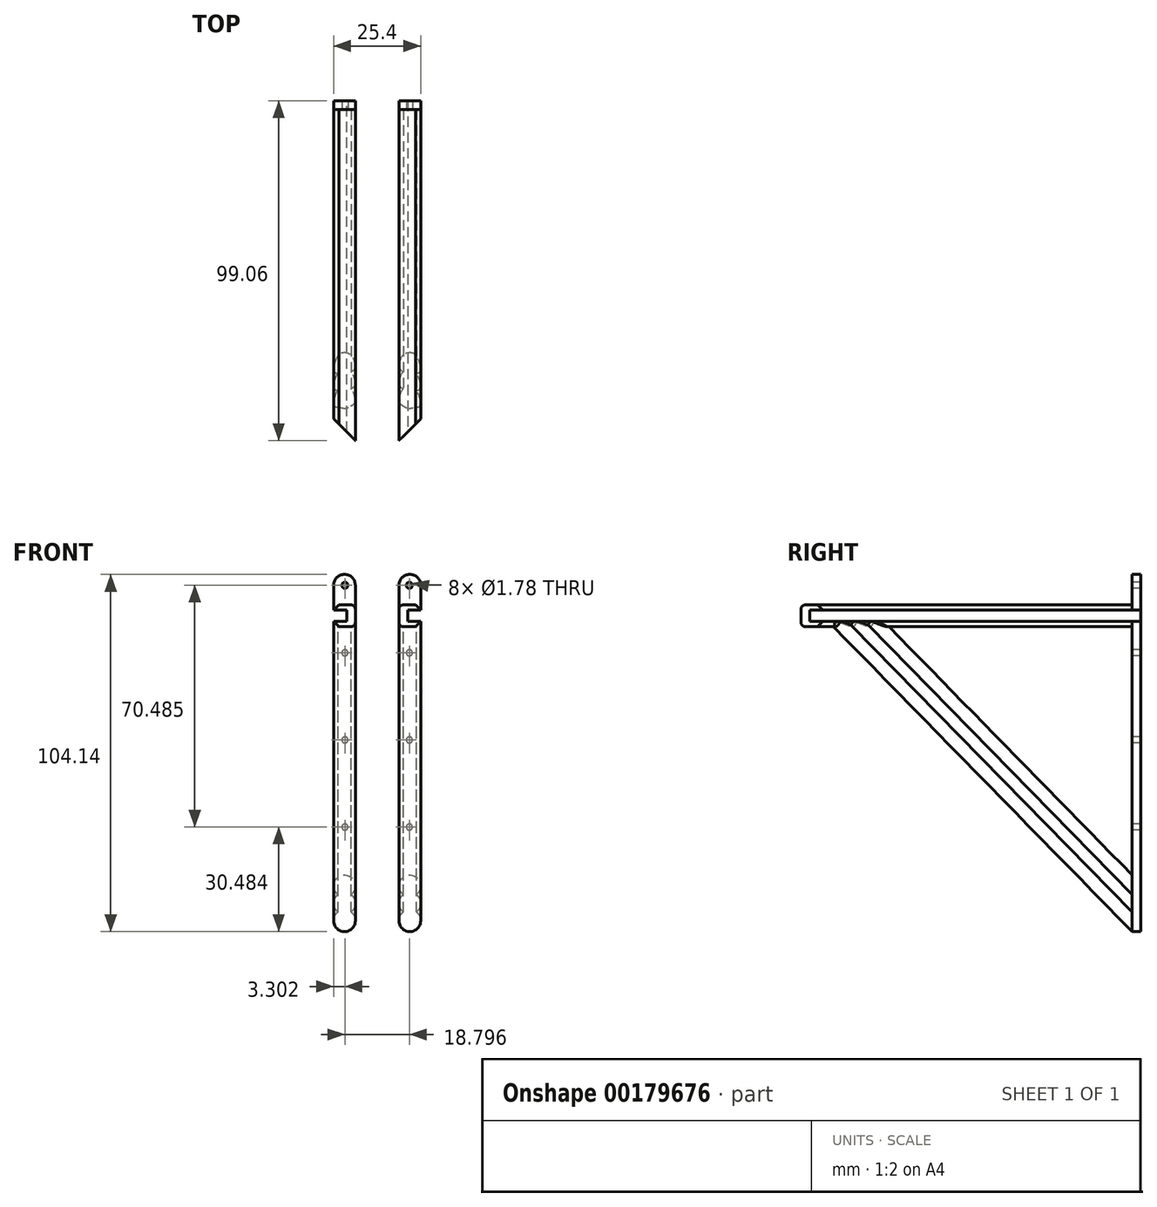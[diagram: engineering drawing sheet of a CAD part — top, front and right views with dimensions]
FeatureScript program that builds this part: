
annotation { "Feature Type Name" : "Feature", "Feature Type Description" : "" }
export const myFeature = defineFeature(function(context is Context, id is Id, definition is map)
    precondition{}
    {
        {
            var Q0;
            Q0=qCreatedBy(makeId("Right.planeOp"),FACE);
            var sketch = newSketch(context, id + "F0", { "sketchPlane" : qUnion([Q0])});
            skLineSegment(sketch, "E0.bottom", {"start": v(-5.81, 6.3) * mm, "end": v(90.7, 6.3) * mm});
            skLineSegment(sketch, "E0.top", {"start": v(-5.81, -0.06) * mm, "end": v(90.7, -0.06) * mm});
            skLineSegment(sketch, "E0.left", {"start": v(-5.81, 6.3) * mm, "end": v(-5.81, -0.06) * mm});
            skLineSegment(sketch, "E0.right", {"start": v(90.7, 6.3) * mm, "end": v(90.7, -0.06) * mm});
            skSolve(sketch);
        }
        {
            var Q0;
            Q0 = qSketchRegion(id + "F0", true);
            extrude(context, id + "F1", {"entities" : qUnion([Q0]), "depth" : 2.54 * mm});
        }
        {
            var Q0;
            Q0=makeQuery(id+"F1.opExtrude","CAP_FACE",FACE,{"disambiguationData":[OSD([sQuery(id+"F0.wireOp",EDGE,"E0.bottom"),sQuery(id+"F0.wireOp",EDGE,"E0.top"),sQuery(id+"F0.wireOp",EDGE,"E0.left"),sQuery(id+"F0.wireOp",EDGE,"E0.right")])],"isStart":false});
            var sketch = newSketch(context, id + "F2", { "sketchPlane" : qUnion([Q0])});
            skLineSegment(sketch, "E1.bottom", {"start": v(-5.81, 6.3) * mm, "end": v(90.7, 6.3) * mm});
            skLineSegment(sketch, "E1.top", {"start": v(-5.81, 4.77) * mm, "end": v(90.7, 4.77) * mm});
            skLineSegment(sketch, "E1.left", {"start": v(-5.81, 6.3) * mm, "end": v(-5.81, 4.77) * mm});
            skLineSegment(sketch, "E1.right", {"start": v(90.7, 6.3) * mm, "end": v(90.7, 4.77) * mm});
            skLineSegment(sketch, "E2.bottom", {"start": v(90.7, -0.06) * mm, "end": v(-5.81, -0.06) * mm});
            skLineSegment(sketch, "E2.top", {"start": v(90.7, 1.52) * mm, "end": v(-5.81, 1.52) * mm});
            skLineSegment(sketch, "E2.left", {"start": v(90.7, -0.06) * mm, "end": v(90.7, 1.52) * mm});
            skLineSegment(sketch, "E2.right", {"start": v(-5.81, -0.06) * mm, "end": v(-5.81, 1.52) * mm});
            skSolve(sketch);
        }
        {
            var Q0;
            Q0 = qSketchRegion(id + "F2", true);
            extrude(context, id + "F3", {"entities" : qUnion([Q0]), "operationType" : NewBodyOperationType.ADD, "depth" : 3.8 * mm});
        }
        {
            var Q0;
            Q0=makeQuery(id+"F3.boolean.opBoolean","MERGE",FACE,{"derivedFrom":[makeQuery(id+"F1.opExtrude","SWEPT_FACE",FACE,{"disambiguationData":[OSD([sQuery(id+"F0.wireOp",EDGE,"E0.bottom")])]}),makeQuery(id+"F3.opExtrude","SWEPT_FACE",FACE,{"disambiguationData":[OSD([sQuery(id+"F2.wireOp",EDGE,"E1.bottom")])]})]});
            var sketch = newSketch(context, id + "F4", { "sketchPlane" : qUnion([Q0])});
            skLineSegment(sketch, "E3", {"start": v(0, -5.81) * mm, "end": v(12.7, -5.81) * mm});
            skLineSegment(sketch, "E4", {"start": v(12.7, -5.81) * mm, "end": v(12.7, 6.89) * mm});
            skLineSegment(sketch, "E5", {"start": v(12.7, 6.89) * mm, "end": v(0, -5.81) * mm});
            skSolve(sketch);
        }
        {
            var Q0;
            Q0 = qSketchRegion(id + "F4", true);
            extrude(context, id + "F5", {"entities" : qUnion([Q0]), "operationType" : NewBodyOperationType.REMOVE, "endBound" : BoundingType.THROUGH_ALL, "oppositeDirection" : true, "depth" : 25.4 * mm});
        }
        {
            var Q0;
            Q0=makeQuery(id+"F3.opExtrude","CAP_EDGE",EDGE,{"disambiguationData":[OSD([sQuery(id+"F2.wireOp",EDGE,"E1.bottom")])],"isStart":false});
            var Q1;
            Q1=makeQuery(id+"F3.opExtrude","CAP_EDGE",EDGE,{"disambiguationData":[OSD([sQuery(id+"F2.wireOp",EDGE,"E2.bottom")])],"isStart":false});
            chamfer(context, id + "F6", {"entities" : qUnion([Q0, Q1]), "width" : 1.52 * mm});
        }
        {
            var Q0;
            Q0=makeQuery(id+"F1.opExtrude","CAP_EDGE",EDGE,{"disambiguationData":[OSD([sQuery(id+"F0.wireOp",EDGE,"E0.bottom")])],"isStart":true});
            var Q1;
            Q1=makeQuery(id+"F1.opExtrude","CAP_EDGE",EDGE,{"disambiguationData":[OSD([sQuery(id+"F0.wireOp",EDGE,"E0.top")])],"isStart":true});
            fillet(context, id + "F7", {"entities" : qUnion([Q0, Q1]), "radius" : 1.27 * mm, "tangentPropagation" : true, "allowEdgeOverflow" : false});
        }
        {
            var Q0;
            Q0=makeQuery(id+"F3.boolean.opBoolean","MERGE",FACE,{"derivedFrom":[makeQuery(id+"F1.opExtrude","SWEPT_FACE",FACE,{"disambiguationData":[OSD([sQuery(id+"F0.wireOp",EDGE,"E0.right")])]}),makeQuery(id+"F3.opExtrude","SWEPT_FACE",FACE,{"disambiguationData":[OSD([sQuery(id+"F2.wireOp",EDGE,"E1.right")])]}),makeQuery(id+"F3.opExtrude","SWEPT_FACE",FACE,{"disambiguationData":[OSD([sQuery(id+"F2.wireOp",EDGE,"E2.left")])]})]});
            var sketch = newSketch(context, id + "F8", { "sketchPlane" : qUnion([Q0])});
            skLineSegment(sketch, "E6.bottom", {"start": v(0, 15.18) * mm, "end": v(-6.35, 15.18) * mm});
            skLineSegment(sketch, "E6.top", {"start": v(0, -88.96) * mm, "end": v(-6.35, -88.96) * mm});
            skLineSegment(sketch, "E6.left", {"start": v(0, 15.18) * mm, "end": v(0, -88.96) * mm});
            skLineSegment(sketch, "E6.right", {"start": v(-6.35, 15.18) * mm, "end": v(-6.35, -88.96) * mm});
            skSolve(sketch);
        }
        {
            var Q0;
            {var subQ6=sQuery(id+"F8.wireOp",EDGE,"E6.top");Q0=makeQuery(id+"F8.imprint","IMPRINT",FACE,{"disambiguationData":[TD([[makeQuery(id+"F8.imprint","IMPRINT",EDGE,{"derivedFrom":subQ6}),-1.0]])]});}
            var Q1;
            {var subQ6=sQuery(id+"F8.wireOp",EDGE,"E6.bottom");Q1=makeQuery(id+"F8.imprint","IMPRINT",FACE,{"disambiguationData":[TD([[makeQuery(id+"F8.imprint","IMPRINT",EDGE,{"derivedFrom":subQ6}),1.0]])]});}
            var Q2;
            {var subQ2=sQuery(id+"F0.wireOp",EDGE,"E0.right");Q2=makeQuery(id+"F8.imprint","IMPRINT",FACE,{"disambiguationData":[TD([[makeQuery(id+"F8.imprint","IMPRINT",EDGE,{"derivedFrom":makeQuery(id+"F1.opExtrude","CAP_EDGE",EDGE,{"disambiguationData":[OSD([subQ2])],"isStart":false})}),1.0]])]});}
            extrude(context, id + "F9", {"entities" : qUnion([Q0, Q1, Q2]), "operationType" : NewBodyOperationType.ADD, "depth" : 2.54 * mm});
        }
        {
            var Q0;
            {var subQ1=sQuery(id+"F0.wireOp",EDGE,"E0.top");var subQ2=sQuery(id+"F2.wireOp",EDGE,"E2.left");var subQ3=sQuery(id+"F2.wireOp",EDGE,"E2.top");var subQ4=sQuery(id+"F0.wireOp",EDGE,"E0.right");var subQ5=sQuery(id+"F8.wireOp",EDGE,"E6.top");var subQ6=sQuery(id+"F8.wireOp",EDGE,"E6.left");var subQ7=sQuery(id+"F8.wireOp",EDGE,"E6.right");var subQ8=sQuery(id+"F2.wireOp",EDGE,"E1.right");Q0=makeQuery(id+"F9.boolean.opBoolean","SPLIT",FACE,{"disambiguationData":[TD([makeQuery(id+"F1.opExtrude","SWEPT_FACE",FACE,{"disambiguationData":[OSD([subQ1])]})])],"derivedFrom":makeQuery(id+"F9.opExtrude","CAP_FACE",FACE,{"disambiguationData":[OSD([subQ4,sQuery(id+"F2.wireOp",EDGE,"E1.top"),subQ8,subQ3,subQ2,sQuery(id+"F8.wireOp",EDGE,"E6.bottom"),subQ5,subQ6,subQ7])],"isStart":true})});}
            var sketch = newSketch(context, id + "F10", { "sketchPlane" : qUnion([Q0])});
            skArc(sketch, "E7", {"start": v(1.27, -83.24) * mm, "mid": v(3.17, -88.96) * mm, "end": v(5.08, -83.24) * mm});
            skPoint(sketch, "E7.centerSnap0", {"position": v(3.18, -88.96) * mm});
            skArc(sketch, "E8", {"start": v(5.08, -83.24) * mm, "mid": v(6.35, -80.7) * mm, "end": v(5.08, -78.16) * mm});
            skArc(sketch, "E9", {"start": v(5.08, -78.16) * mm, "mid": v(3.17, -72.45) * mm, "end": v(1.27, -78.16) * mm});
            skPoint(sketch, "E9.centerSnap0", {"position": v(3.17, -77.53) * mm});
            skArc(sketch, "E10.trimOffspring", {"start": v(1.27, -78.16) * mm, "mid": v(0, -80.7) * mm, "end": v(1.27, -83.24) * mm});
            skSolve(sketch);
        }
        {
            var Q0;
            {var subQ0=sQuery(id+"F8.wireOp",EDGE,"E6.right");var subQ1=sQuery(id+"F2.wireOp",EDGE,"E2.left");var subQ2=sQuery(id+"F2.wireOp",EDGE,"E2.top");var subQ3=sQuery(id+"F0.wireOp",EDGE,"E0.right");var subQ4=sQuery(id+"F2.wireOp",EDGE,"E2.bottom");Q0=makeQuery(id+"F9.boolean.opBoolean","MERGE",FACE,{"derivedFrom":[makeQuery(id+"F3.opExtrude","CAP_FACE",FACE,{"disambiguationData":[OSD([subQ4,subQ2,subQ1,sQuery(id+"F2.wireOp",EDGE,"E2.right")])],"isStart":false}),makeQuery(id+"F9.opExtrude","SWEPT_FACE",FACE,{"disambiguationData":[OSD([subQ0]),TDD([makeQuery(id+"F8.imprint","IMPRINT",EDGE,{"disambiguationData":[TD([[makeQuery(id+"F8.imprint","INTERSECT",VERTEX,{"derivedFrom":[sQuery(id+"F8.wireOp",EDGE,"E6.top"),subQ0]}),1.0]])],"derivedFrom":subQ0}),makeQuery(id+"F8.imprint","IMPRINT",EDGE,{"disambiguationData":[TD([[makeQuery(id+"F8.imprint","INTERSECT",VERTEX,{"derivedFrom":[makeQuery(id+"F3.opExtrude","SWEPT_EDGE",EDGE,{"disambiguationData":[OSD([subQ3,subQ2,subQ1])]}),subQ0]}),-1.0]])],"derivedFrom":subQ0})])]})]});}
            var Q1;
            Q1=makeQuery(id+"F9.boolean.opBoolean","MERGE",FACE,{"derivedFrom":[makeQuery(id+"F1.opExtrude","CAP_FACE",FACE,{"disambiguationData":[OSD([sQuery(id+"F0.wireOp",EDGE,"E0.bottom"),sQuery(id+"F0.wireOp",EDGE,"E0.top"),sQuery(id+"F0.wireOp",EDGE,"E0.left"),sQuery(id+"F0.wireOp",EDGE,"E0.right")])],"isStart":true}),makeQuery(id+"F9.opExtrude","SWEPT_FACE",FACE,{"disambiguationData":[OSD([sQuery(id+"F8.wireOp",EDGE,"E6.left")])]})]});
            cPlane(context, id + "F11", {"entities" : qUnion([Q0, Q1]), "cplaneType" : CPlaneType.MID_PLANE, "offset" : 25.4 * mm, "width" : 152.4 * mm, "height" : 152.4 * mm});
        }
        {
            var Q0;
            Q0=qCreatedBy(id+"F11.planeOp",FACE);
            var sketch = newSketch(context, id + "F12", { "sketchPlane" : qUnion([Q0])});
            skLineSegment(sketch, "E11", {"start": v(90.7, -88.96) * mm, "end": v(3.58, 0) * mm});
            skSolve(sketch);
        }
        {
            var Q0;
            {var subQ1=sQuery(id+"F10.wireOp",EDGE,"E7");var subQ9=sQuery(id+"F8.wireOp",EDGE,"E6.top");var subQ12=makeQuery(id+"F10.imprint","INTERSECT",VERTEX,{"derivedFrom":[makeQuery(id+"F9.opExtrude","CAP_EDGE",EDGE,{"disambiguationData":[OSD([subQ9])],"isStart":true}),subQ1]});Q0=makeQuery(id+"F10.imprint","IMPRINT",FACE,{"disambiguationData":[TD([[makeQuery(id+"F10.imprint","IMPRINT",EDGE,{"disambiguationData":[TD([[subQ12,-1.0]])],"derivedFrom":subQ1}),1.0]])]});}
            var Q1;
            Q1=sQuery(id+"F12.wireOp",EDGE,"E11");
            sweep(context, id + "F13", {"operationType" : NewBodyOperationType.ADD, "profiles" : qUnion([Q0]), "path" : qUnion([Q1])});
        }
        {
            var Q0;
            {var subQ0=sQuery(id+"F2.wireOp",EDGE,"E1.top");var subQ3=sQuery(id+"F10.wireOp",EDGE,"E7");Q0=makeQuery(id+"F13.boolean.opBoolean","SPLIT",FACE,{"disambiguationData":[TD([makeQuery(id+"F3.opExtrude","SWEPT_FACE",FACE,{"disambiguationData":[OSD([subQ0])]})])],"derivedFrom":makeQuery(id+"F13.opSweep","CAP_FACE",FACE,{"disambiguationData":[OSD([subQ3,sQuery(id+"F10.wireOp",EDGE,"E8"),sQuery(id+"F12.wireOp",VERTEX,"E11.end")])],"isStart":false})});}
            var sketch = newSketch(context, id + "F14", { "sketchPlane" : qUnion([Q0])});
            skLineSegment(sketch, "E12", {"start": v(6.35, 4.77) * mm, "end": v(2.54, 4.77) * mm});
            skLineSegment(sketch, "E13", {"start": v(2.54, 4.77) * mm, "end": v(2.54, 1.52) * mm});
            skLineSegment(sketch, "E14", {"start": v(2.54, 1.52) * mm, "end": v(6.35, 1.52) * mm});
            skLineSegment(sketch, "E15", {"start": v(6.35, 1.52) * mm, "end": v(8.34, 2.97) * mm});
            skLineSegment(sketch, "E16", {"start": v(8.34, 2.97) * mm, "end": v(6.35, 4.77) * mm});
            skLineSegment(sketch, "E17", {"start": v(6.35, 4.77) * mm, "end": v(4.83, 6.3) * mm});
            skLineSegment(sketch, "E18", {"start": v(4.83, 6.3) * mm, "end": v(1.27, 6.3) * mm});
            skArc(sketch, "E19", {"start": v(1.27, 6.3) * mm, "mid": v(0.37, 5.92) * mm, "end": v(0, 5.02) * mm});
            skLineSegment(sketch, "E20", {"start": v(0, 5.02) * mm, "end": v(0, 17.72) * mm});
            skLineSegment(sketch, "E21", {"start": v(0, 17.72) * mm, "end": v(9.04, 18.27) * mm});
            skLineSegment(sketch, "E22", {"start": v(9.04, 18.27) * mm, "end": v(6.35, 4.77) * mm});
            skSolve(sketch);
        }
        {
            var Q0;
            Q0 = qSketchRegion(id + "F14", true);
            extrude(context, id + "F15", {"entities" : qUnion([Q0]), "operationType" : NewBodyOperationType.REMOVE, "oppositeDirection" : true, "depth" : 25.4 * mm});
        }
        {
            var Q0;
            {var subQ0=sQuery(id+"F2.wireOp",EDGE,"E2.bottom");var subQ1=makeQuery(id+"F3.opExtrude","SWEPT_FACE",FACE,{"disambiguationData":[OSD([subQ0])]});var subQ2=sQuery(id+"F8.wireOp",EDGE,"E6.right");var subQ3=sQuery(id+"F8.wireOp",EDGE,"E6.left");var subQ4=sQuery(id+"F8.wireOp",EDGE,"E6.top");var subQ5=sQuery(id+"F2.wireOp",EDGE,"E2.left");var subQ6=sQuery(id+"F2.wireOp",EDGE,"E2.top");var subQ7=sQuery(id+"F2.wireOp",EDGE,"E1.right");var subQ8=sQuery(id+"F0.wireOp",EDGE,"E0.right");var subQ9=makeQuery(id+"F9.opExtrude","CAP_FACE",FACE,{"disambiguationData":[OSD([subQ8,sQuery(id+"F2.wireOp",EDGE,"E1.top"),subQ7,subQ6,subQ5,sQuery(id+"F8.wireOp",EDGE,"E6.bottom"),subQ4,subQ3,subQ2])],"isStart":true});var subQ10=sQuery(id+"F0.wireOp",EDGE,"E0.top");var subQ11=makeQuery(id+"F1.opExtrude","SWEPT_FACE",FACE,{"disambiguationData":[OSD([subQ10])]});var subQ12=makeQuery(id+"F3.opExtrude","CAP_FACE",FACE,{"disambiguationData":[OSD([subQ0,subQ6,subQ5,sQuery(id+"F2.wireOp",EDGE,"E2.right")])],"isStart":false});var subQ13=makeQuery(id+"F1.opExtrude","CAP_FACE",FACE,{"disambiguationData":[OSD([sQuery(id+"F0.wireOp",EDGE,"E0.bottom"),subQ10,sQuery(id+"F0.wireOp",EDGE,"E0.left"),subQ8])],"isStart":true});var subQ14=makeQuery(id+"F6.opChamfer","BLEND_FACE",FACE,{"disambiguationData":[OSD([subQ0])]});var subQ15=makeQuery(id+"F7.opFillet","BLEND_FACE",FACE,{"disambiguationData":[OSD([subQ10])]});var subQ16=makeQuery(id+"F9.opExtrude","SWEPT_FACE",FACE,{"disambiguationData":[OSD([subQ3])]});var subQ18=makeQuery(id+"F9.opExtrude","SWEPT_FACE",FACE,{"disambiguationData":[OSD([subQ2]),TDD([makeQuery(id+"F8.imprint","IMPRINT",EDGE,{"disambiguationData":[TD([[makeQuery(id+"F8.imprint","INTERSECT",VERTEX,{"derivedFrom":[subQ4,subQ2]}),1.0]])],"derivedFrom":subQ2}),makeQuery(id+"F8.imprint","IMPRINT",EDGE,{"disambiguationData":[TD([[makeQuery(id+"F8.imprint","INTERSECT",VERTEX,{"derivedFrom":[makeQuery(id+"F3.opExtrude","SWEPT_EDGE",EDGE,{"disambiguationData":[OSD([subQ8,subQ6,subQ5])]}),subQ2]}),-1.0]])],"derivedFrom":subQ2})])]});Q0=makeQuery(id+"F13.boolean.opBoolean","SPLIT",FACE,{"disambiguationData":[TD([subQ13,subQ11,subQ1,subQ12,subQ14,subQ15,subQ9,subQ16,subQ18,makeQuery(id+"F13.opSweep","SWEPT_FACE",FACE,{"disambiguationData":[OSD([sQuery(id+"F10.wireOp",EDGE,"E8"),sQuery(id+"F12.wireOp",EDGE,"E11")])]})])],"derivedFrom":makeQuery(id+"F9.boolean.opBoolean","SPLIT",FACE,{"disambiguationData":[TD([subQ11])],"derivedFrom":subQ9})});}
            var sketch = newSketch(context, id + "F16", { "sketchPlane" : qUnion([Q0])});
            skCircle(sketch, "E23", {"center": v(3.05, 12) * mm, "radius": 0.89 * mm});
            skPoint(sketch, "E23.centerSnap0", {"position": v(3.05, -0.06) * mm});
            skCircle(sketch, "E24", {"center": v(3.05, -7.68) * mm, "radius": 0.89 * mm});
            skCircle(sketch, "E25", {"center": v(3.05, -33.08) * mm, "radius": 0.89 * mm});
            skCircle(sketch, "E26", {"center": v(3.05, -58.48) * mm, "radius": 0.89 * mm});
            skSolve(sketch);
        }
        {
            var Q0;
            Q0 = qSketchRegion(id + "F16", true);
            extrude(context, id + "F17", {"entities" : qUnion([Q0]), "operationType" : NewBodyOperationType.REMOVE, "oppositeDirection" : true, "depth" : 25.4 * mm});
        }
        {
            var Q0;
            Q0=makeQuery(id+"F9.opExtrude","SWEPT_EDGE",EDGE,{"disambiguationData":[OSD([sQuery(id+"F8.wireOp",EDGE,"E6.bottom"),sQuery(id+"F8.wireOp",EDGE,"E6.right")])]});
            var Q1;
            Q1=makeQuery(id+"F9.opExtrude","SWEPT_EDGE",EDGE,{"disambiguationData":[OSD([sQuery(id+"F8.wireOp",EDGE,"E6.bottom"),sQuery(id+"F8.wireOp",EDGE,"E6.left")])]});
            var Q2;
            Q2=makeQuery(id+"F9.opExtrude","SWEPT_EDGE",EDGE,{"disambiguationData":[OSD([sQuery(id+"F8.wireOp",EDGE,"E6.top"),sQuery(id+"F8.wireOp",EDGE,"E6.right")])]});
            var Q3;
            Q3=makeQuery(id+"F9.opExtrude","SWEPT_EDGE",EDGE,{"disambiguationData":[OSD([sQuery(id+"F8.wireOp",EDGE,"E6.top"),sQuery(id+"F8.wireOp",EDGE,"E6.left")])]});
            fillet(context, id + "F18", {"entities" : qUnion([Q0, Q1, Q2, Q3]), "radius" : 3.17 * mm, "tangentPropagation" : true, "allowEdgeOverflow" : false});
        }
        {
            var Q0;
            Q0=qCreatedBy(makeId("Right.planeOp"),FACE);
            cPlane(context, id + "F19", {"entities" : qUnion([Q0]), "cplaneType" : CPlaneType.OFFSET, "offset" : 6.35 * mm, "oppositeDirection" : true, "width" : 152.4 * mm, "height" : 152.4 * mm});
        }
        {
            var Q0;
            Q0=makeQuery(id+"F1.opExtrude","SWEPT_BODY",BODY,{"disambiguationData":[OSD([sQuery(id+"F0.wireOp",EDGE,"E0.bottom"),sQuery(id+"F0.wireOp",EDGE,"E0.top"),sQuery(id+"F0.wireOp",EDGE,"E0.left"),sQuery(id+"F0.wireOp",EDGE,"E0.right")])]});
            var Q1;
            Q1=qCreatedBy(id+"F19.planeOp",FACE);
            mirror(context, id + "F20", {"entities" : qUnion([Q0]), "mirrorPlane" : qUnion([Q1])});
        }
    });
